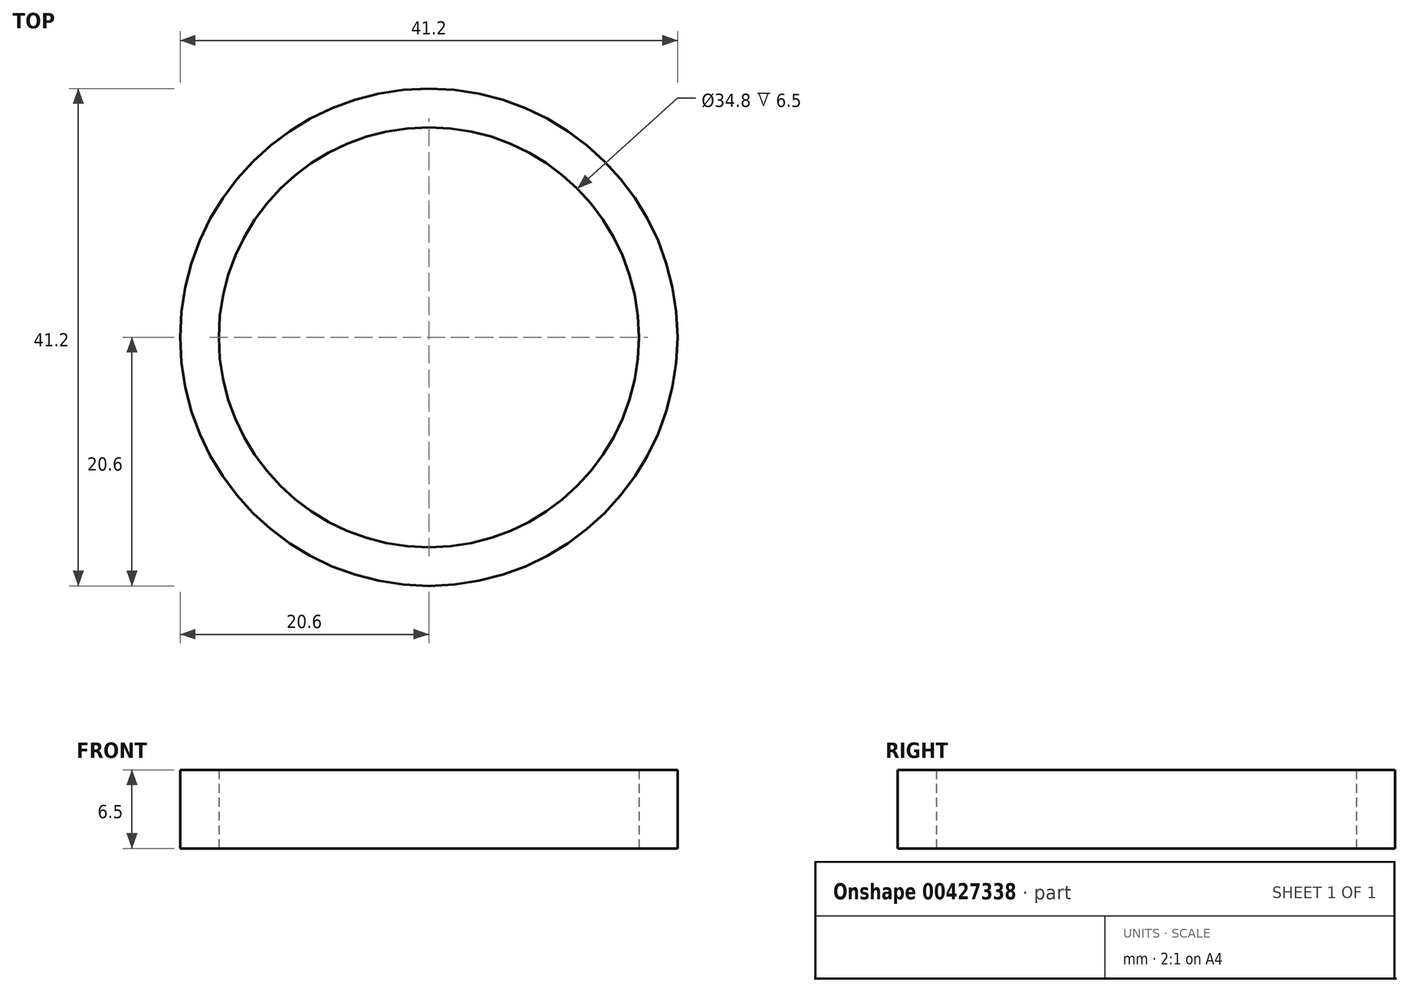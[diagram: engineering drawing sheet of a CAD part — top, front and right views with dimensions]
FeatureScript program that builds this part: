
annotation { "Feature Type Name" : "Feature", "Feature Type Description" : "" }
export const myFeature = defineFeature(function(context is Context, id is Id, definition is map)
    precondition{}
    {
        {
            var Q0;
            Q0=qCreatedBy(makeId("Top.planeOp"),FACE);
            var sketch = newSketch(context, id + "F0", { "sketchPlane" : qUnion([Q0])});
            skCircle(sketch, "E0", {"center": v(0, 0) * mm, "radius": 17.4 * mm});
            skCircle(sketch, "E1", {"center": v(0, 0) * mm, "radius": 20.6 * mm});
            skSolve(sketch);
        }
        {
            var Q0;
            Q0 = qSketchRegion(id + "F0", true);
            extrude(context, id + "F1", {"entities" : qUnion([Q0]), "depth" : 6.5 * mm});
        }
    });
